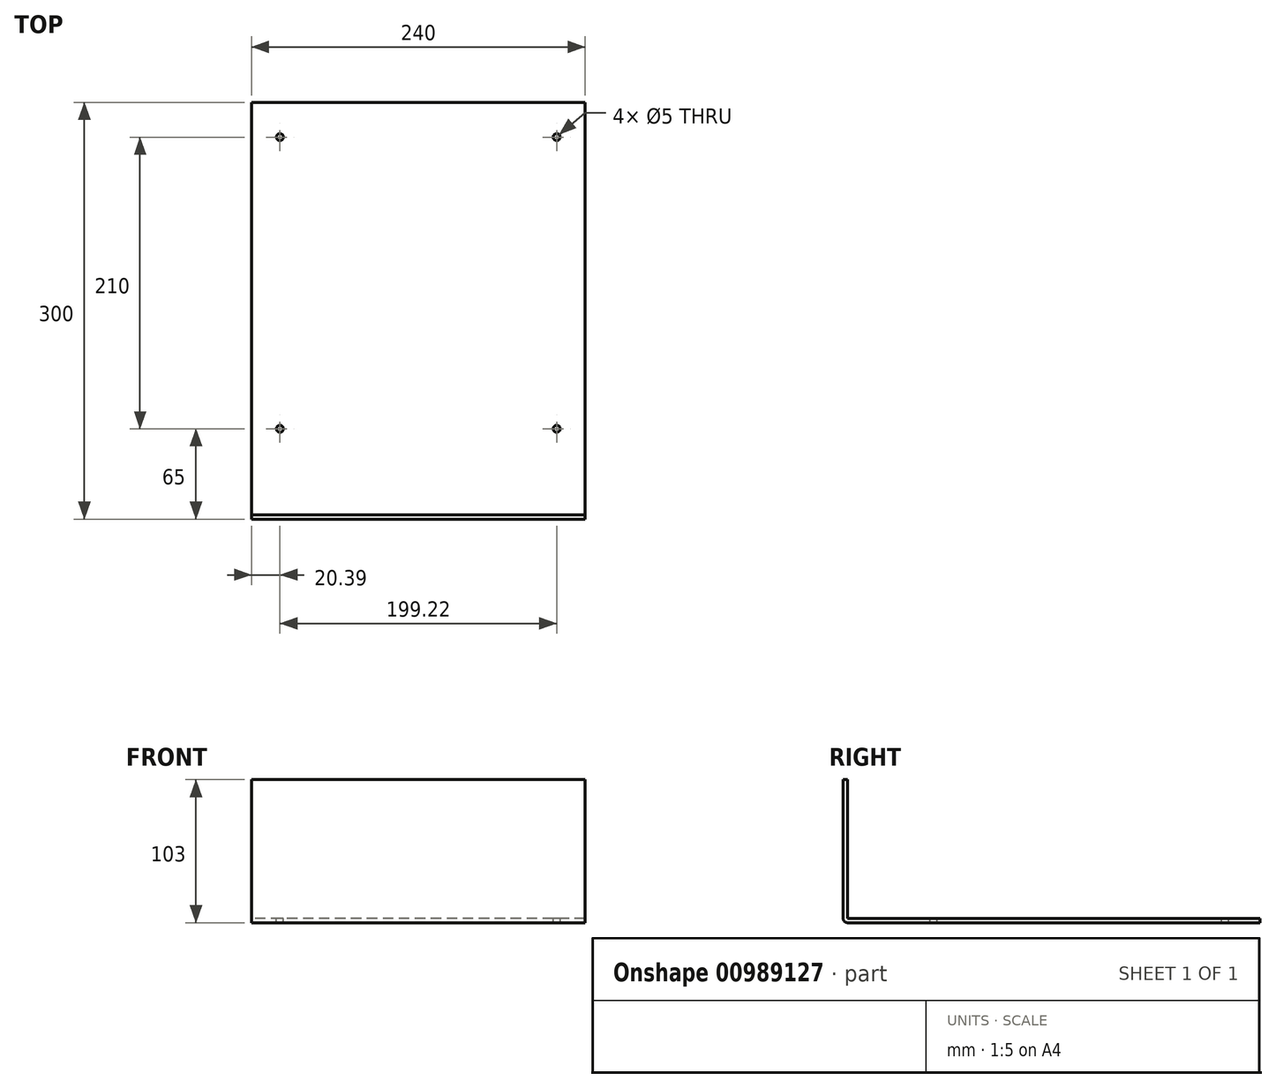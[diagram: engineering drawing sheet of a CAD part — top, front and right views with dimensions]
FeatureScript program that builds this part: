
annotation { "Feature Type Name" : "Feature", "Feature Type Description" : "" }
export const myFeature = defineFeature(function(context is Context, id is Id, definition is map)
    precondition{}
    {
        {
            var Q0;
            Q0=qCreatedBy(makeId("Front.planeOp"),FACE);
            var sketch = newSketch(context, id + "F0", { "sketchPlane" : qUnion([Q0])});
            skLineSegment(sketch, "E0.bottom", {"start": v(120, 1.5) * mm, "end": v(-120, 1.5) * mm});
            skLineSegment(sketch, "E0.top", {"start": v(120, -1.5) * mm, "end": v(-120, -1.5) * mm});
            skLineSegment(sketch, "E0.left", {"start": v(120, 1.5) * mm, "end": v(120, -1.5) * mm});
            skLineSegment(sketch, "E0.right", {"start": v(-120, 1.5) * mm, "end": v(-120, -1.5) * mm});
            skPoint(sketch, "E0.middle", {"position": v(0, 0) * mm});
            skSolve(sketch);
        }
        {
            var Q0;
            Q0 = qSketchRegion(id + "F0", true);
            extrude(context, id + "F1", {"entities" : qUnion([Q0]), "depth" : 300 * mm, "offsetDistance" : 25 * mm});
        }
        {
            var Q0;
            Q0=makeQuery(id+"F1.opExtrude","SWEPT_FACE",FACE,{"disambiguationData":[OSD([sQuery(id+"F0.wireOp",EDGE,"E0.bottom")])]});
            var sketch = newSketch(context, id + "F2", { "sketchPlane" : qUnion([Q0])});
            skLineSegment(sketch, "E1", {"start": v(-120, -25) * mm, "end": v(120, -25) * mm});
            skPoint(sketch, "E2", {"position": v(-99.61, -25) * mm});
            skPoint(sketch, "E3", {"position": v(99.61, -25) * mm});
            skLineSegment(sketch, "E4", {"start": v(-120, -235) * mm, "end": v(120, -235) * mm});
            skPoint(sketch, "E5", {"position": v(-99.61, -235) * mm});
            skPoint(sketch, "E6", {"position": v(99.6, -235) * mm});
            skCircle(sketch, "E7", {"center": v(-99.61, -25) * mm, "radius": 2.5 * mm});
            skCircle(sketch, "E8", {"center": v(99.61, -25) * mm, "radius": 2.5 * mm});
            skCircle(sketch, "E9", {"center": v(99.6, -235) * mm, "radius": 2.5 * mm});
            skCircle(sketch, "E10", {"center": v(-99.61, -235) * mm, "radius": 2.5 * mm});
            skSolve(sketch);
        }
        {
            var Q0;
            Q0 = qSketchRegion(id + "F2", true);
            extrude(context, id + "F3", {"entities" : qUnion([Q0]), "operationType" : NewBodyOperationType.REMOVE, "oppositeDirection" : true, "depth" : 25 * mm, "offsetDistance" : 25 * mm});
        }
        {
            var Q0;
            Q0=makeQuery(id+"F1.opExtrude","SWEPT_FACE",FACE,{"disambiguationData":[OSD([sQuery(id+"F0.wireOp",EDGE,"E0.bottom")])]});
            var sketch = newSketch(context, id + "F4", { "sketchPlane" : qUnion([Q0])});
            skLineSegment(sketch, "E11.bottom", {"start": v(120, -297) * mm, "end": v(-120, -297) * mm});
            skLineSegment(sketch, "E11.top", {"start": v(120, -300) * mm, "end": v(-120, -300) * mm});
            skLineSegment(sketch, "E11.left", {"start": v(120, -297) * mm, "end": v(120, -300) * mm});
            skLineSegment(sketch, "E11.right", {"start": v(-120, -297) * mm, "end": v(-120, -300) * mm});
            skPoint(sketch, "E11.middle", {"position": v(0, -298.5) * mm});
            skSolve(sketch);
        }
        {
            var Q0;
            Q0 = qSketchRegion(id + "F4", true);
            extrude(context, id + "F5", {"entities" : qUnion([Q0]), "operationType" : NewBodyOperationType.ADD, "depth" : 100 * mm, "offsetDistance" : 25 * mm});
        }
        {
            var Q0;
            Q0=makeQuery(id+"F5.opExtrude","CAP_EDGE",EDGE,{"disambiguationData":[OSD([sQuery(id+"F4.wireOp",EDGE,"E11.bottom")])],"isStart":true});
            var Q1;
            Q1=makeQuery(id+"F1.opExtrude","CAP_EDGE",EDGE,{"disambiguationData":[OSD([sQuery(id+"F0.wireOp",EDGE,"E0.top")])],"isStart":false});
            fillet(context, id + "F6", {"entities" : qUnion([Q0, Q1]), "radius" : 3 * mm, "tangentPropagation" : true, "allowEdgeOverflow" : false});
        }
    });
